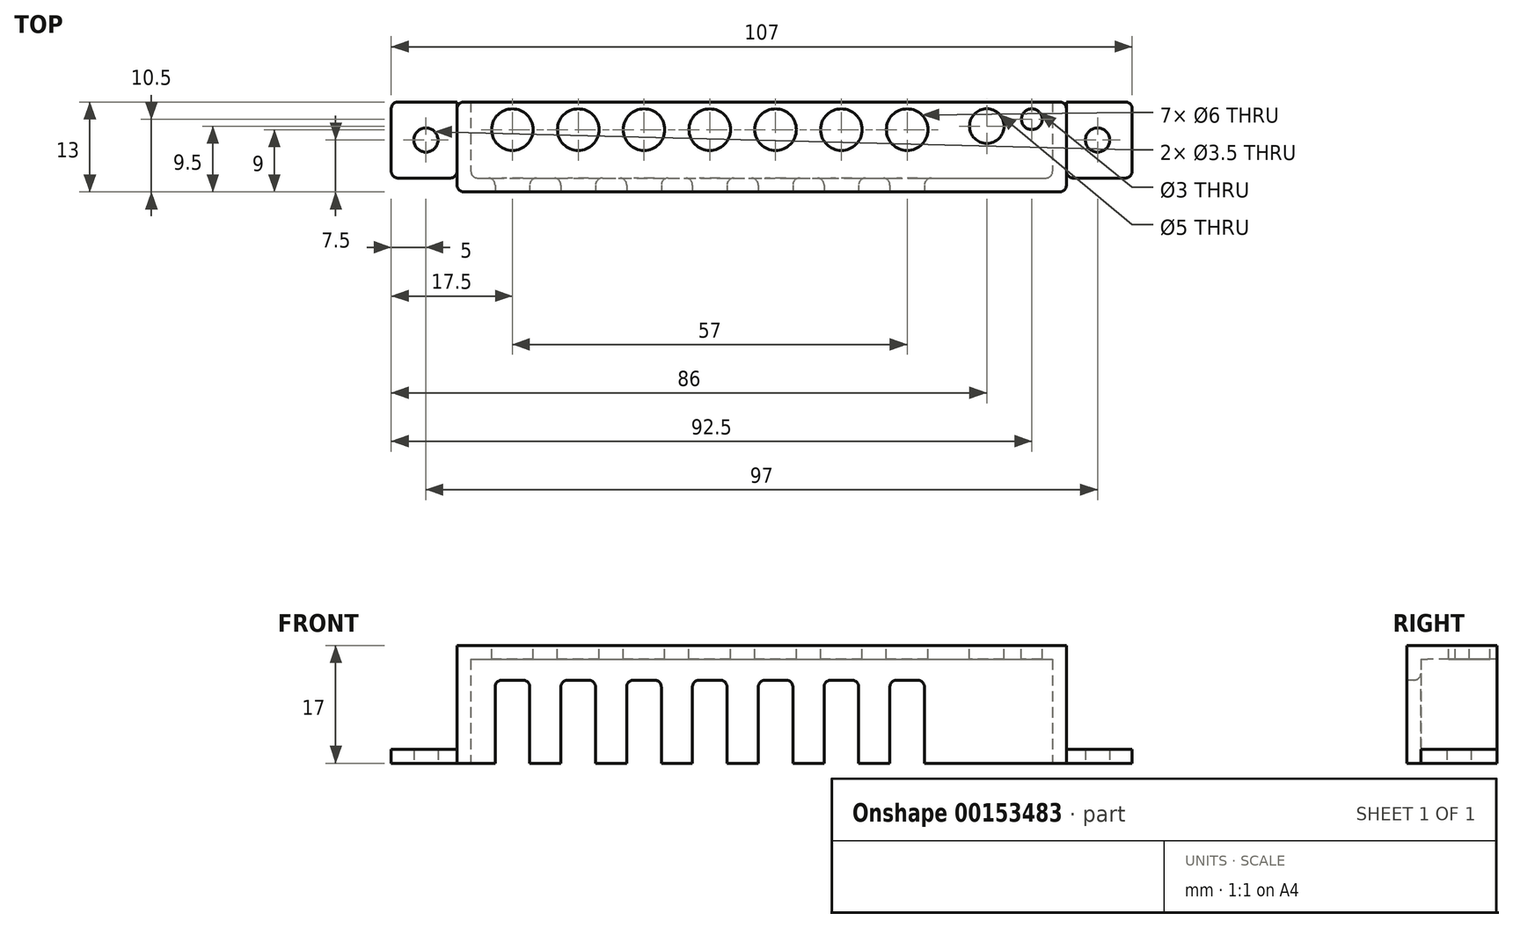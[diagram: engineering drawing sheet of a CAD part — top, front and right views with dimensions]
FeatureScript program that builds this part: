
annotation { "Feature Type Name" : "Feature", "Feature Type Description" : "" }
export const myFeature = defineFeature(function(context is Context, id is Id, definition is map)
    precondition{}
    {
        {
            var Q0;
            Q0=qCreatedBy(makeId("Top.planeOp"),FACE);
            var sketch = newSketch(context, id + "F0", { "sketchPlane" : qUnion([Q0])});
            skLineSegment(sketch, "E0.bottom", {"start": v(-55.5, 23) * mm, "end": v(51.5, 23) * mm});
            skLineSegment(sketch, "E0.top", {"start": v(-55.5, 12) * mm, "end": v(-46, 12) * mm});
            skLineSegment(sketch, "E0.left", {"start": v(-55.5, 23) * mm, "end": v(-55.5, 12) * mm});
            skLineSegment(sketch, "E0.right", {"start": v(51.5, 23) * mm, "end": v(51.5, 12) * mm});
            skLineSegment(sketch, "E1.bottom", {"start": v(-46, 23) * mm, "end": v(42, 23) * mm});
            skLineSegment(sketch, "E1.top", {"start": v(-46, 10) * mm, "end": v(42, 10) * mm});
            skLineSegment(sketch, "E1.left", {"start": v(-46, 23) * mm, "end": v(-46, 10) * mm});
            skLineSegment(sketch, "E1.right", {"start": v(42, 23) * mm, "end": v(42, 10) * mm});
            skLineSegment(sketch, "E2", {"start": v(-44, 23) * mm, "end": v(-44, 12) * mm});
            skLineSegment(sketch, "E3", {"start": v(40, 23) * mm, "end": v(40, 12) * mm});
            skLineSegment(sketch, "E4.trimOffspring", {"start": v(-44, 12) * mm, "end": v(40, 12) * mm});
            skLineSegment(sketch, "E5.trimOffspring", {"start": v(42, 12) * mm, "end": v(51.5, 12) * mm});
            skCircle(sketch, "E6", {"center": v(-50.5, 17.5) * mm, "radius": 1.75 * mm});
            skCircle(sketch, "E7", {"center": v(46.5, 17.5) * mm, "radius": 1.75 * mm});
            skSolve(sketch);
        }
        {
            var Q0;
            {var subQ4=sQuery(id+"F0.wireOp",EDGE,"E0.right");Q0=makeQuery(id+"F0.imprint","IMPRINT",FACE,{"disambiguationData":[TD([[makeQuery(id+"F0.imprint","IMPRINT",EDGE,{"derivedFrom":subQ4}),-1.0]])]});}
            var Q1;
            {var subQ1=sQuery(id+"F0.wireOp",EDGE,"E0.top");Q1=makeQuery(id+"F0.imprint","IMPRINT",FACE,{"disambiguationData":[TD([[makeQuery(id+"F0.imprint","IMPRINT",EDGE,{"derivedFrom":subQ1}),1.0]])]});}
            extrude(context, id + "F1", {"entities" : qUnion([Q0, Q1]), "depth" : 2 * mm});
        }
        {
            var Q0;
            {var subQ5=sQuery(id+"F0.wireOp",EDGE,"E1.top");Q0=makeQuery(id+"F0.imprint","IMPRINT",FACE,{"disambiguationData":[TD([[makeQuery(id+"F0.imprint","IMPRINT",EDGE,{"derivedFrom":subQ5}),1.0]])]});}
            extrude(context, id + "F2", {"entities" : qUnion([Q0]), "depth" : 17 * mm});
        }
        {
            var Q0;
            {var subQ0=sQuery(id+"F0.wireOp",EDGE,"E2");Q0=makeQuery(id+"F0.imprint","IMPRINT",FACE,{"disambiguationData":[TD([[makeQuery(id+"F0.imprint","IMPRINT",EDGE,{"derivedFrom":subQ0}),1.0]])]});}
            extrude(context, id + "F3", {"entities" : qUnion([Q0]), "operationType" : NewBodyOperationType.ADD, "depth" : 17 * mm});
        }
        {
            var Q0;
            {var subQ0=sQuery(id+"F0.wireOp",EDGE,"E2");Q0=makeQuery(id+"F0.imprint","IMPRINT",FACE,{"disambiguationData":[TD([[makeQuery(id+"F0.imprint","IMPRINT",EDGE,{"derivedFrom":subQ0}),1.0]])]});}
            extrude(context, id + "F4", {"entities" : qUnion([Q0]), "operationType" : NewBodyOperationType.REMOVE, "depth" : 15 * mm});
        }
        {
            var Q0;
            Q0=makeQuery(id+"F2.opExtrude","SWEPT_FACE",FACE,{"disambiguationData":[OSD([sQuery(id+"F0.wireOp",EDGE,"E1.top")])]});
            var sketch = newSketch(context, id + "F5", { "sketchPlane" : qUnion([Q0])});
            skLineSegment(sketch, "E8.bottom", {"start": v(-39.5, 12) * mm, "end": v(-36.5, 12) * mm});
            skLineSegment(sketch, "E8.top", {"start": v(-40.5, 0) * mm, "end": v(-35.5, 0) * mm});
            skLineSegment(sketch, "E8.left", {"start": v(-40.5, 11) * mm, "end": v(-40.5, 0) * mm});
            skLineSegment(sketch, "E8.right", {"start": v(-35.5, 11) * mm, "end": v(-35.5, 0) * mm});
            skLineSegment(sketch, "E9.bottom", {"start": v(-30, 12) * mm, "end": v(-27, 12) * mm});
            skLineSegment(sketch, "E9.top", {"start": v(-31, 0) * mm, "end": v(-26, 0) * mm});
            skLineSegment(sketch, "E9.left", {"start": v(-31, 11) * mm, "end": v(-31, 0) * mm});
            skLineSegment(sketch, "E9.right", {"start": v(-26, 11) * mm, "end": v(-26, 0) * mm});
            skLineSegment(sketch, "E10.bottom", {"start": v(-20.5, 12) * mm, "end": v(-17.5, 12) * mm});
            skLineSegment(sketch, "E10.top", {"start": v(-21.5, 0) * mm, "end": v(-16.5, 0) * mm});
            skLineSegment(sketch, "E10.left", {"start": v(-21.5, 11) * mm, "end": v(-21.5, 0) * mm});
            skLineSegment(sketch, "E10.right", {"start": v(-16.5, 11) * mm, "end": v(-16.5, 0) * mm});
            skLineSegment(sketch, "E11.bottom", {"start": v(-11, 12) * mm, "end": v(-8, 12) * mm});
            skLineSegment(sketch, "E11.top", {"start": v(-12, 0) * mm, "end": v(-7, 0) * mm});
            skLineSegment(sketch, "E11.left", {"start": v(-12, 11) * mm, "end": v(-12, 0) * mm});
            skLineSegment(sketch, "E11.right", {"start": v(-7, 11) * mm, "end": v(-7, 0) * mm});
            skLineSegment(sketch, "E12.bottom", {"start": v(-1.5, 12) * mm, "end": v(1.5, 12) * mm});
            skLineSegment(sketch, "E12.top", {"start": v(-2.5, 0) * mm, "end": v(2.5, 0) * mm});
            skLineSegment(sketch, "E12.left", {"start": v(-2.5, 11) * mm, "end": v(-2.5, 0) * mm});
            skLineSegment(sketch, "E12.right", {"start": v(2.5, 11) * mm, "end": v(2.5, 0) * mm});
            skLineSegment(sketch, "E13.bottom", {"start": v(8, 12) * mm, "end": v(11, 12) * mm});
            skLineSegment(sketch, "E13.top", {"start": v(7, 0) * mm, "end": v(12, 0) * mm});
            skLineSegment(sketch, "E13.left", {"start": v(7, 11) * mm, "end": v(7, 0) * mm});
            skLineSegment(sketch, "E13.right", {"start": v(12, 11) * mm, "end": v(12, 0) * mm});
            skLineSegment(sketch, "E14.bottom", {"start": v(17.5, 12) * mm, "end": v(20.5, 12) * mm});
            skLineSegment(sketch, "E14.top", {"start": v(16.5, 0) * mm, "end": v(21.5, 0) * mm});
            skLineSegment(sketch, "E14.left", {"start": v(16.5, 11) * mm, "end": v(16.5, 0) * mm});
            skLineSegment(sketch, "E14.right", {"start": v(21.5, 11) * mm, "end": v(21.5, 0) * mm});
            skPoint(sketch, "E15.visualSharp", {"position": v(-40.5, 12) * mm});
            skArc(sketch, "E15.filletArc", {"start": v(-39.5, 12) * mm, "mid": v(-40.2, 11.7) * mm, "end": v(-40.5, 11) * mm});
            skPoint(sketch, "E16.visualSharp", {"position": v(-35.5, 12) * mm});
            skArc(sketch, "E16.filletArc", {"start": v(-35.5, 11) * mm, "mid": v(-35.8, 11.7) * mm, "end": v(-36.5, 12) * mm});
            skPoint(sketch, "E17.visualSharp", {"position": v(-31, 12) * mm});
            skArc(sketch, "E17.filletArc", {"start": v(-30, 12) * mm, "mid": v(-30.7, 11.7) * mm, "end": v(-31, 11) * mm});
            skPoint(sketch, "E18.visualSharp", {"position": v(-26, 12) * mm});
            skArc(sketch, "E18.filletArc", {"start": v(-26, 11) * mm, "mid": v(-26.3, 11.7) * mm, "end": v(-27, 12) * mm});
            skPoint(sketch, "E19.visualSharp", {"position": v(-21.5, 12) * mm});
            skArc(sketch, "E19.filletArc", {"start": v(-20.5, 12) * mm, "mid": v(-21.2, 11.7) * mm, "end": v(-21.5, 11) * mm});
            skPoint(sketch, "E20.visualSharp", {"position": v(-12, 12) * mm});
            skArc(sketch, "E20.filletArc", {"start": v(-11, 12) * mm, "mid": v(-11.7, 11.7) * mm, "end": v(-12, 11) * mm});
            skPoint(sketch, "E21.visualSharp", {"position": v(-7, 12) * mm});
            skArc(sketch, "E21.filletArc", {"start": v(-7, 11) * mm, "mid": v(-7.3, 11.7) * mm, "end": v(-8, 12) * mm});
            skPoint(sketch, "E22.visualSharp", {"position": v(-2.5, 12) * mm});
            skArc(sketch, "E22.filletArc", {"start": v(-1.5, 12) * mm, "mid": v(-2.2, 11.7) * mm, "end": v(-2.5, 11) * mm});
            skPoint(sketch, "E23.visualSharp", {"position": v(2.5, 12) * mm});
            skArc(sketch, "E23.filletArc", {"start": v(2.5, 11) * mm, "mid": v(2.2, 11.7) * mm, "end": v(1.5, 12) * mm});
            skPoint(sketch, "E24.visualSharp", {"position": v(7, 12) * mm});
            skArc(sketch, "E24.filletArc", {"start": v(8, 12) * mm, "mid": v(7.3, 11.7) * mm, "end": v(7, 11) * mm});
            skPoint(sketch, "E25.visualSharp", {"position": v(12, 12) * mm});
            skArc(sketch, "E25.filletArc", {"start": v(12, 11) * mm, "mid": v(11.7, 11.7) * mm, "end": v(11, 12) * mm});
            skPoint(sketch, "E26.visualSharp", {"position": v(16.5, 12) * mm});
            skArc(sketch, "E26.filletArc", {"start": v(17.5, 12) * mm, "mid": v(16.8, 11.7) * mm, "end": v(16.5, 11) * mm});
            skPoint(sketch, "E27.visualSharp", {"position": v(21.5, 12) * mm});
            skArc(sketch, "E27.filletArc", {"start": v(21.5, 11) * mm, "mid": v(21.2, 11.7) * mm, "end": v(20.5, 12) * mm});
            skPoint(sketch, "E28.visualSharp", {"position": v(-16.5, 12) * mm});
            skArc(sketch, "E28.filletArc", {"start": v(-16.5, 11) * mm, "mid": v(-16.8, 11.7) * mm, "end": v(-17.5, 12) * mm});
            skSolve(sketch);
        }
        {
            var Q0;
            Q0=makeQuery(id+"F5.imprint","IMPRINT",FACE,{"disambiguationData":[TD([[makeQuery(id+"F5.imprint","IMPRINT",EDGE,{"derivedFrom":sQuery(id+"F5.wireOp",EDGE,"E8.bottom")}),-1.0]])]});
            var Q1;
            Q1=makeQuery(id+"F5.imprint","IMPRINT",FACE,{"disambiguationData":[TD([[makeQuery(id+"F5.imprint","IMPRINT",EDGE,{"derivedFrom":sQuery(id+"F5.wireOp",EDGE,"E9.bottom")}),-1.0]])]});
            var Q2;
            Q2=makeQuery(id+"F5.imprint","IMPRINT",FACE,{"disambiguationData":[TD([[makeQuery(id+"F5.imprint","IMPRINT",EDGE,{"derivedFrom":sQuery(id+"F5.wireOp",EDGE,"E10.bottom")}),-1.0]])]});
            var Q3;
            Q3=makeQuery(id+"F5.imprint","IMPRINT",FACE,{"disambiguationData":[TD([[makeQuery(id+"F5.imprint","IMPRINT",EDGE,{"derivedFrom":sQuery(id+"F5.wireOp",EDGE,"E11.bottom")}),-1.0]])]});
            var Q4;
            Q4=makeQuery(id+"F5.imprint","IMPRINT",FACE,{"disambiguationData":[TD([[makeQuery(id+"F5.imprint","IMPRINT",EDGE,{"derivedFrom":sQuery(id+"F5.wireOp",EDGE,"E12.bottom")}),-1.0]])]});
            var Q5;
            Q5=makeQuery(id+"F5.imprint","IMPRINT",FACE,{"disambiguationData":[TD([[makeQuery(id+"F5.imprint","IMPRINT",EDGE,{"derivedFrom":sQuery(id+"F5.wireOp",EDGE,"E13.bottom")}),-1.0]])]});
            var Q6;
            Q6=makeQuery(id+"F5.imprint","IMPRINT",FACE,{"disambiguationData":[TD([[makeQuery(id+"F5.imprint","IMPRINT",EDGE,{"derivedFrom":sQuery(id+"F5.wireOp",EDGE,"E14.bottom")}),-1.0]])]});
            extrude(context, id + "F6", {"entities" : qUnion([Q0, Q1, Q2, Q3, Q4, Q5, Q6]), "operationType" : NewBodyOperationType.REMOVE, "endBound" : BoundingType.THROUGH_ALL, "oppositeDirection" : true, "depth" : 25 * mm});
        }
        {
            var Q0;
            {var subQ0=sQuery(id+"F0.wireOp",EDGE,"E4.trimOffspring");var subQ1=sQuery(id+"F0.wireOp",EDGE,"E3");var subQ2=sQuery(id+"F0.wireOp",EDGE,"E2");var subQ3=sQuery(id+"F0.wireOp",EDGE,"E1.bottom");Q0=makeQuery(id+"F3.boolean.opBoolean","MERGE",FACE,{"derivedFrom":[makeQuery(id+"F2.opExtrude","CAP_FACE",FACE,{"disambiguationData":[OSD([subQ3,sQuery(id+"F0.wireOp",EDGE,"E1.top"),sQuery(id+"F0.wireOp",EDGE,"E1.left"),sQuery(id+"F0.wireOp",EDGE,"E1.right"),subQ2,subQ1,subQ0])],"isStart":false}),makeQuery(id+"F3.opExtrude","CAP_FACE",FACE,{"disambiguationData":[OSD([subQ3,subQ2,subQ1,subQ0])],"isStart":false})]});}
            var sketch = newSketch(context, id + "F7", { "sketchPlane" : qUnion([Q0])});
            skCircle(sketch, "E29", {"center": v(-38, 19) * mm, "radius": 3 * mm});
            skCircle(sketch, "E30.1.0.0", {"center": v(-28.5, 19) * mm, "radius": 3 * mm});
            skCircle(sketch, "E30.2.0.0", {"center": v(-19, 19) * mm, "radius": 3 * mm});
            skCircle(sketch, "E30.3.0.0", {"center": v(-9.5, 19) * mm, "radius": 3 * mm});
            skCircle(sketch, "E30.4.0.0", {"center": v(0, 19) * mm, "radius": 3 * mm});
            skCircle(sketch, "E30.5.0.0", {"center": v(9.5, 19) * mm, "radius": 3 * mm});
            skCircle(sketch, "E30.6.0.0", {"center": v(19, 19) * mm, "radius": 3 * mm});
            skLineSegment(sketch, "E30.direction1", {"start": v(-38, 19) * mm, "end": v(-28.5, 19) * mm, "construction": true});
            skCircle(sketch, "E31", {"center": v(37, 20.5) * mm, "radius": 1.5 * mm});
            skCircle(sketch, "E32", {"center": v(30.5, 19.5) * mm, "radius": 2.5 * mm});
            skSolve(sketch);
        }
        {
            var Q0;
            Q0=makeQuery(id+"F7.imprint","IMPRINT",FACE,{"disambiguationData":[TD([[makeQuery(id+"F7.imprint","IMPRINT",EDGE,{"derivedFrom":sQuery(id+"F7.wireOp",EDGE,"E29")}),1.0]])]});
            var Q1;
            Q1=makeQuery(id+"F7.imprint","IMPRINT",FACE,{"disambiguationData":[TD([[makeQuery(id+"F7.imprint","IMPRINT",EDGE,{"derivedFrom":sQuery(id+"F7.wireOp",EDGE,"E30.1.0.0")}),1.0]])]});
            var Q2;
            Q2=makeQuery(id+"F7.imprint","IMPRINT",FACE,{"disambiguationData":[TD([[makeQuery(id+"F7.imprint","IMPRINT",EDGE,{"derivedFrom":sQuery(id+"F7.wireOp",EDGE,"E30.2.0.0")}),1.0]])]});
            var Q3;
            Q3=makeQuery(id+"F7.imprint","IMPRINT",FACE,{"disambiguationData":[TD([[makeQuery(id+"F7.imprint","IMPRINT",EDGE,{"derivedFrom":sQuery(id+"F7.wireOp",EDGE,"E30.3.0.0")}),1.0]])]});
            var Q4;
            Q4=makeQuery(id+"F7.imprint","IMPRINT",FACE,{"disambiguationData":[TD([[makeQuery(id+"F7.imprint","IMPRINT",EDGE,{"derivedFrom":sQuery(id+"F7.wireOp",EDGE,"E30.5.0.0")}),1.0]])]});
            var Q5;
            Q5=makeQuery(id+"F7.imprint","IMPRINT",FACE,{"disambiguationData":[TD([[makeQuery(id+"F7.imprint","IMPRINT",EDGE,{"derivedFrom":sQuery(id+"F7.wireOp",EDGE,"E30.6.0.0")}),1.0]])]});
            var Q6;
            Q6=makeQuery(id+"F7.imprint","IMPRINT",FACE,{"disambiguationData":[TD([[makeQuery(id+"F7.imprint","IMPRINT",EDGE,{"derivedFrom":sQuery(id+"F7.wireOp",EDGE,"E32")}),1.0]])]});
            var Q7;
            Q7=makeQuery(id+"F7.imprint","IMPRINT",FACE,{"disambiguationData":[TD([[makeQuery(id+"F7.imprint","IMPRINT",EDGE,{"derivedFrom":sQuery(id+"F7.wireOp",EDGE,"E31")}),1.0]])]});
            var Q8;
            Q8=makeQuery(id+"F7.imprint","IMPRINT",FACE,{"disambiguationData":[TD([[makeQuery(id+"F7.imprint","IMPRINT",EDGE,{"derivedFrom":sQuery(id+"F7.wireOp",EDGE,"E30.4.0.0")}),1.0]])]});
            extrude(context, id + "F8", {"entities" : qUnion([Q0, Q1, Q2, Q3, Q4, Q5, Q6, Q7, Q8]), "operationType" : NewBodyOperationType.REMOVE, "oppositeDirection" : true, "depth" : 25 * mm});
        }
        {
            var Q0;
            Q0=makeQuery(id+"F6.boolean.opBoolean","COPY",EDGE,{"derivedFrom":makeQuery(id+"F6.opExtrude","CAP_EDGE",EDGE,{"disambiguationData":[OSD([sQuery(id+"F5.wireOp",EDGE,"E8.left")])],"isStart":true})});
            var Q1;
            Q1=makeQuery(id+"F6.boolean.opBoolean","INTERSECT",EDGE,{"derivedFrom":[makeQuery(id+"F4.boolean.opBoolean","COPY",FACE,{"derivedFrom":makeQuery(id+"F4.opExtrude","SWEPT_FACE",FACE,{"disambiguationData":[OSD([sQuery(id+"F0.wireOp",EDGE,"E4.trimOffspring")])]})}),makeQuery(id+"F6.opExtrude","SWEPT_FACE",FACE,{"disambiguationData":[OSD([sQuery(id+"F5.wireOp",EDGE,"E8.left")])]})]});
            var Q2;
            Q2=makeQuery(id+"F6.boolean.opBoolean","COPY",EDGE,{"derivedFrom":makeQuery(id+"F6.opExtrude","CAP_EDGE",EDGE,{"disambiguationData":[OSD([sQuery(id+"F5.wireOp",EDGE,"E9.left")])],"isStart":true})});
            var Q3;
            Q3=makeQuery(id+"F6.boolean.opBoolean","INTERSECT",EDGE,{"derivedFrom":[makeQuery(id+"F4.boolean.opBoolean","COPY",FACE,{"derivedFrom":makeQuery(id+"F4.opExtrude","SWEPT_FACE",FACE,{"disambiguationData":[OSD([sQuery(id+"F0.wireOp",EDGE,"E4.trimOffspring")])]})}),makeQuery(id+"F6.opExtrude","SWEPT_FACE",FACE,{"disambiguationData":[OSD([sQuery(id+"F5.wireOp",EDGE,"E9.left")])]})]});
            var Q4;
            Q4=makeQuery(id+"F6.boolean.opBoolean","COPY",EDGE,{"derivedFrom":makeQuery(id+"F6.opExtrude","CAP_EDGE",EDGE,{"disambiguationData":[OSD([sQuery(id+"F5.wireOp",EDGE,"E10.left")])],"isStart":true})});
            var Q5;
            Q5=makeQuery(id+"F6.boolean.opBoolean","INTERSECT",EDGE,{"derivedFrom":[makeQuery(id+"F4.boolean.opBoolean","COPY",FACE,{"derivedFrom":makeQuery(id+"F4.opExtrude","SWEPT_FACE",FACE,{"disambiguationData":[OSD([sQuery(id+"F0.wireOp",EDGE,"E4.trimOffspring")])]})}),makeQuery(id+"F6.opExtrude","SWEPT_FACE",FACE,{"disambiguationData":[OSD([sQuery(id+"F5.wireOp",EDGE,"E10.left")])]})]});
            var Q6;
            Q6=makeQuery(id+"F6.boolean.opBoolean","COPY",EDGE,{"derivedFrom":makeQuery(id+"F6.opExtrude","CAP_EDGE",EDGE,{"disambiguationData":[OSD([sQuery(id+"F5.wireOp",EDGE,"E11.left")])],"isStart":true})});
            var Q7;
            Q7=makeQuery(id+"F6.boolean.opBoolean","INTERSECT",EDGE,{"derivedFrom":[makeQuery(id+"F4.boolean.opBoolean","COPY",FACE,{"derivedFrom":makeQuery(id+"F4.opExtrude","SWEPT_FACE",FACE,{"disambiguationData":[OSD([sQuery(id+"F0.wireOp",EDGE,"E4.trimOffspring")])]})}),makeQuery(id+"F6.opExtrude","SWEPT_FACE",FACE,{"disambiguationData":[OSD([sQuery(id+"F5.wireOp",EDGE,"E11.left")])]})]});
            var Q8;
            Q8=makeQuery(id+"F6.boolean.opBoolean","COPY",EDGE,{"derivedFrom":makeQuery(id+"F6.opExtrude","CAP_EDGE",EDGE,{"disambiguationData":[OSD([sQuery(id+"F5.wireOp",EDGE,"E12.left")])],"isStart":true})});
            var Q9;
            Q9=makeQuery(id+"F6.boolean.opBoolean","INTERSECT",EDGE,{"derivedFrom":[makeQuery(id+"F4.boolean.opBoolean","COPY",FACE,{"derivedFrom":makeQuery(id+"F4.opExtrude","SWEPT_FACE",FACE,{"disambiguationData":[OSD([sQuery(id+"F0.wireOp",EDGE,"E4.trimOffspring")])]})}),makeQuery(id+"F6.opExtrude","SWEPT_FACE",FACE,{"disambiguationData":[OSD([sQuery(id+"F5.wireOp",EDGE,"E12.left")])]})]});
            var Q10;
            Q10=makeQuery(id+"F6.boolean.opBoolean","COPY",EDGE,{"derivedFrom":makeQuery(id+"F6.opExtrude","CAP_EDGE",EDGE,{"disambiguationData":[OSD([sQuery(id+"F5.wireOp",EDGE,"E13.left")])],"isStart":true})});
            var Q11;
            Q11=makeQuery(id+"F6.boolean.opBoolean","INTERSECT",EDGE,{"derivedFrom":[makeQuery(id+"F4.boolean.opBoolean","COPY",FACE,{"derivedFrom":makeQuery(id+"F4.opExtrude","SWEPT_FACE",FACE,{"disambiguationData":[OSD([sQuery(id+"F0.wireOp",EDGE,"E4.trimOffspring")])]})}),makeQuery(id+"F6.opExtrude","SWEPT_FACE",FACE,{"disambiguationData":[OSD([sQuery(id+"F5.wireOp",EDGE,"E13.left")])]})]});
            var Q12;
            Q12=makeQuery(id+"F6.boolean.opBoolean","COPY",EDGE,{"derivedFrom":makeQuery(id+"F6.opExtrude","CAP_EDGE",EDGE,{"disambiguationData":[OSD([sQuery(id+"F5.wireOp",EDGE,"E14.left")])],"isStart":true})});
            var Q13;
            Q13=makeQuery(id+"F6.boolean.opBoolean","INTERSECT",EDGE,{"derivedFrom":[makeQuery(id+"F4.boolean.opBoolean","COPY",FACE,{"derivedFrom":makeQuery(id+"F4.opExtrude","SWEPT_FACE",FACE,{"disambiguationData":[OSD([sQuery(id+"F0.wireOp",EDGE,"E4.trimOffspring")])]})}),makeQuery(id+"F6.opExtrude","SWEPT_FACE",FACE,{"disambiguationData":[OSD([sQuery(id+"F5.wireOp",EDGE,"E14.left")])]})]});
            fillet(context, id + "F9", {"entities" : qUnion([Q0, Q1, Q2, Q3, Q4, Q5, Q6, Q7, Q8, Q9, Q10, Q11, Q12, Q13]), "radius" : 1 * mm, "tangentPropagation" : true, "allowEdgeOverflow" : false});
        }
        {
            var Q0;
            Q0=makeQuery(id+"F2.opExtrude","SWEPT_EDGE",EDGE,{"disambiguationData":[OSD([sQuery(id+"F0.wireOp",EDGE,"E1.top"),sQuery(id+"F0.wireOp",EDGE,"E1.left")])]});
            var Q1;
            Q1=makeQuery(id+"F1.opExtrude","SWEPT_EDGE",EDGE,{"disambiguationData":[OSD([sQuery(id+"F0.wireOp",EDGE,"E0.top"),sQuery(id+"F0.wireOp",EDGE,"E1.left")])]});
            var Q2;
            Q2=makeQuery(id+"F1.opExtrude","SWEPT_EDGE",EDGE,{"disambiguationData":[OSD([sQuery(id+"F0.wireOp",EDGE,"E0.top"),sQuery(id+"F0.wireOp",EDGE,"E0.left")])]});
            var Q3;
            Q3=makeQuery(id+"F1.opExtrude","SWEPT_EDGE",EDGE,{"disambiguationData":[OSD([sQuery(id+"F0.wireOp",EDGE,"E0.bottom"),sQuery(id+"F0.wireOp",EDGE,"E0.left")])]});
            var Q4;
            Q4=makeQuery(id+"F2.opExtrude","SWEPT_EDGE",EDGE,{"disambiguationData":[OSD([sQuery(id+"F0.wireOp",EDGE,"E0.bottom"),sQuery(id+"F0.wireOp",EDGE,"E1.bottom"),sQuery(id+"F0.wireOp",EDGE,"E1.left")])]});
            var Q5;
            Q5=makeQuery(id+"F4.boolean.opBoolean","COPY",EDGE,{"derivedFrom":makeQuery(id+"F4.opExtrude","SWEPT_EDGE",EDGE,{"disambiguationData":[OSD([sQuery(id+"F0.wireOp",EDGE,"E1.bottom"),sQuery(id+"F0.wireOp",EDGE,"E2")])]})});
            var Q6;
            Q6=makeQuery(id+"F4.boolean.opBoolean","COPY",EDGE,{"derivedFrom":makeQuery(id+"F4.opExtrude","SWEPT_EDGE",EDGE,{"disambiguationData":[OSD([sQuery(id+"F0.wireOp",EDGE,"E1.bottom"),sQuery(id+"F0.wireOp",EDGE,"E3")])]})});
            var Q7;
            Q7=makeQuery(id+"F2.opExtrude","SWEPT_EDGE",EDGE,{"disambiguationData":[OSD([sQuery(id+"F0.wireOp",EDGE,"E0.bottom"),sQuery(id+"F0.wireOp",EDGE,"E1.bottom"),sQuery(id+"F0.wireOp",EDGE,"E1.right")])]});
            var Q8;
            Q8=makeQuery(id+"F1.opExtrude","SWEPT_EDGE",EDGE,{"disambiguationData":[OSD([sQuery(id+"F0.wireOp",EDGE,"E0.bottom"),sQuery(id+"F0.wireOp",EDGE,"E0.right")])]});
            var Q9;
            Q9=makeQuery(id+"F1.opExtrude","SWEPT_EDGE",EDGE,{"disambiguationData":[OSD([sQuery(id+"F0.wireOp",EDGE,"E0.right"),sQuery(id+"F0.wireOp",EDGE,"E5.trimOffspring")])]});
            var Q10;
            Q10=makeQuery(id+"F2.opExtrude","SWEPT_EDGE",EDGE,{"disambiguationData":[OSD([sQuery(id+"F0.wireOp",EDGE,"E1.top"),sQuery(id+"F0.wireOp",EDGE,"E1.right")])]});
            var Q11;
            Q11=makeQuery(id+"F1.opExtrude","SWEPT_EDGE",EDGE,{"disambiguationData":[OSD([sQuery(id+"F0.wireOp",EDGE,"E1.right"),sQuery(id+"F0.wireOp",EDGE,"E5.trimOffspring")])]});
            var Q12;
            Q12=makeQuery(id+"F4.boolean.opBoolean","COPY",EDGE,{"derivedFrom":makeQuery(id+"F4.opExtrude","SWEPT_EDGE",EDGE,{"disambiguationData":[OSD([sQuery(id+"F0.wireOp",EDGE,"E3"),sQuery(id+"F0.wireOp",EDGE,"E4.trimOffspring")])]})});
            var Q13;
            Q13=makeQuery(id+"F4.boolean.opBoolean","COPY",EDGE,{"derivedFrom":makeQuery(id+"F4.opExtrude","SWEPT_EDGE",EDGE,{"disambiguationData":[OSD([sQuery(id+"F0.wireOp",EDGE,"E2"),sQuery(id+"F0.wireOp",EDGE,"E4.trimOffspring")])]})});
            fillet(context, id + "F10", {"entities" : qUnion([Q0, Q1, Q2, Q3, Q4, Q5, Q6, Q7, Q8, Q9, Q10, Q11, Q12, Q13]), "radius" : 1 * mm, "tangentPropagation" : true, "allowEdgeOverflow" : false});
        }
    });
